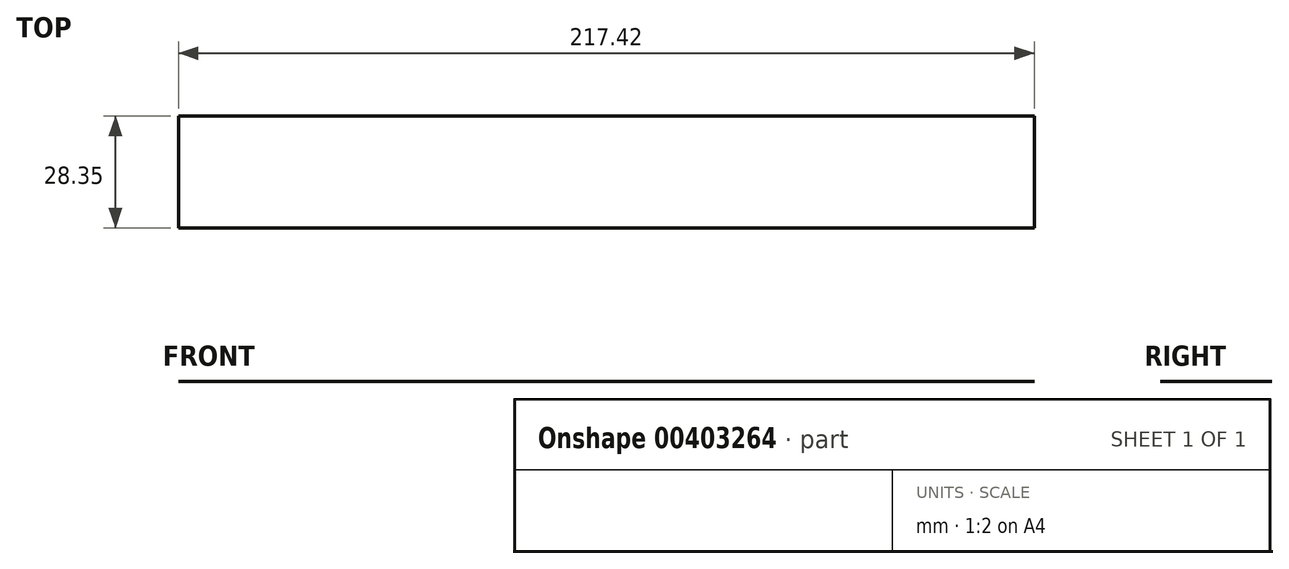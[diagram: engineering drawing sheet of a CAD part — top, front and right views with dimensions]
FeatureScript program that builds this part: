
annotation { "Feature Type Name" : "Feature", "Feature Type Description" : "" }
export const myFeature = defineFeature(function(context is Context, id is Id, definition is map)
    precondition{}
    {
        {
            var Q0;
            Q0=qCreatedBy(makeId("Right.planeOp"),FACE);
            var sketch = newSketch(context, id + "F0", { "sketchPlane" : qUnion([Q0])});
            skLineSegment(sketch, "E0.bottom", {"start": v(-48.17, 48.92) * mm, "end": v(-19.82, 48.92) * mm});
            skLineSegment(sketch, "E0.top", {"start": v(-48.17, 6.52) * mm, "end": v(-19.82, 6.52) * mm});
            skLineSegment(sketch, "E0.left", {"start": v(-48.17, 48.92) * mm, "end": v(-48.17, 6.52) * mm});
            skLineSegment(sketch, "E0.right", {"start": v(-19.82, 48.92) * mm, "end": v(-19.82, 6.52) * mm});
            skSolve(sketch);
        }
        {
            var Q0;
            Q0 = qSketchRegion(id + "F0", true);
            var Q1;
            Q1=sQuery(id+"F0.wireOp",EDGE,"E0.bottom");
            extrude(context, id + "F1", {"entities" : qUnion([Q0]), "bodyType" : ToolBodyType.SURFACE, "surfaceEntities" : qUnion([Q1]), "depth" : 217.42 * mm});
        }
    });
